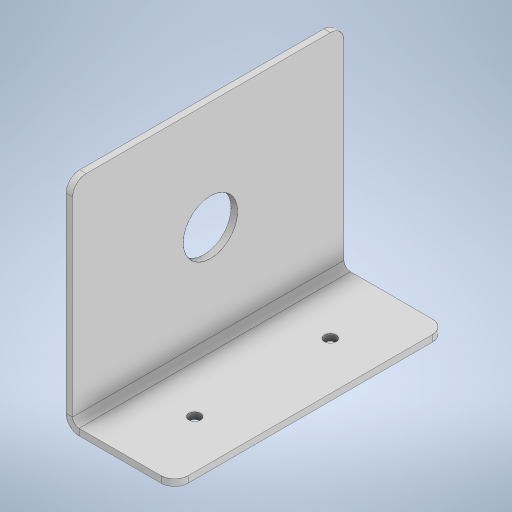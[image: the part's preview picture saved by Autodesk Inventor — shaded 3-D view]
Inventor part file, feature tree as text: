
AUTODESK INVENTOR PART (.ipt)
format: ipt  version: 2023 (Build 270158030, 158C)  size: 255,488 bytes
history: native  units: in
note: dims shown in document units (in); Inventor stores cm internally (conversion verified against a paired STEP export)
features: sheet_metal_op x4, sketch x4, hole x2, other x2, chamfer x1
ambient origin geometry x8: Origin, YZ Plane, XZ Plane, XY Plane, X Axis, Y Axis, Z Axis, Center Point
bodies: Solid1 (feature_tree)
feature tree (13):
  sheet_metal_op  "Face1"
  sheet_metal_op  "Flange1"
  hole  "Hole1"  [1 undecoded]
  chamfer  "Corner Round1"
  hole  "Hole2"  [1 undecoded]
  sketch  "Sketch1"  dims[d0=2.0in d1=5.0in]
  other  "Plate1"
  sketch  "Sketch2"  dims[d2=0.12in d3=0.12in]
  other  "Plate2"
  sheet_metal_op  "Bend1"
  sheet_metal_op  "Corner1"
  sketch  "Sketch3"  dims[d4=0.06in]
  sketch  "Sketch4"  dims[d5=0.24in d6=0.12in d7=4.0in d8=90.0deg d9=0.12in d10=0.48in d11=0.12in d12=0.12in d13=0.217in d14=0.75in d15=0.2559in d16=0.1024in d17=0.5635in d18=0.12in d19=0.8108in d20=2.5in d21=1.25in d22=0.25in d23=2.54in d24=1.0in d25=0.75in d26=0.591in d27=0.169in d28=0.5635in d29=1.0in d30=0.8108in d31=2.0in]
note: 2 required parameter values undecoded (feature->parameter linkage not recoverable at this tier; creation-order binding heuristic only, values carry confidence <= 0.55)
